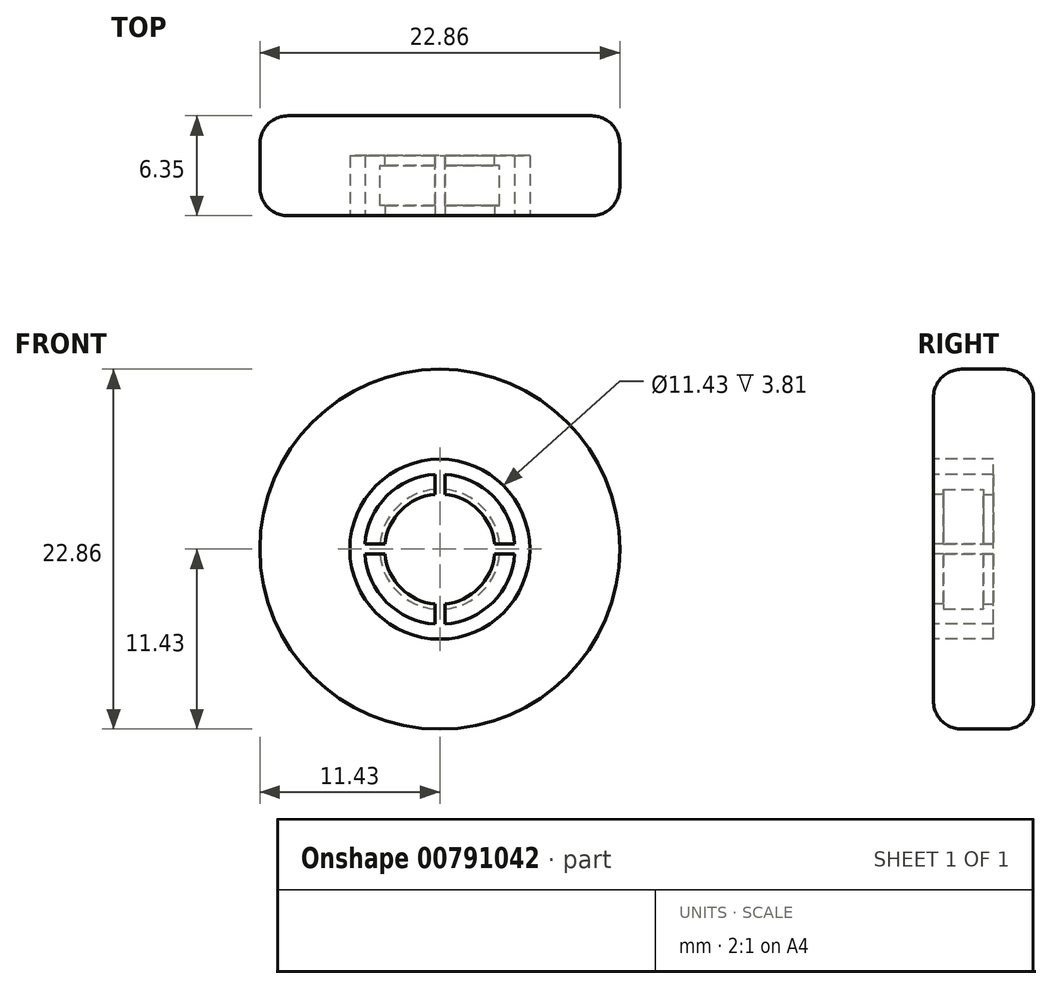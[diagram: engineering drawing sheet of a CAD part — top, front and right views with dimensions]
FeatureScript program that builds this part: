
annotation { "Feature Type Name" : "Feature", "Feature Type Description" : "" }
export const myFeature = defineFeature(function(context is Context, id is Id, definition is map)
    precondition{}
    {
        {
            var Q0;
            Q0=qCreatedBy(makeId("Front.planeOp"),FACE);
            var sketch = newSketch(context, id + "F0", { "sketchPlane" : qUnion([Q0])});
            skCircle(sketch, "E0", {"center": v(0, 0) * mm, "radius": 11.43 * mm});
            skSolve(sketch);
        }
        {
            var Q0;
            Q0=makeQuery(id+"F0.imprint","IMPRINT",FACE,{"disambiguationData":[TD([[makeQuery(id+"F0.imprint","IMPRINT",EDGE,{"derivedFrom":sQuery(id+"F0.wireOp",EDGE,"E0")}),1.0]])]});
            extrude(context, id + "F1", {"entities" : qUnion([Q0]), "depth" : 6.35 * mm, "offsetDistance" : 25.4 * mm});
        }
        {
            var Q0;
            Q0=makeQuery(id+"F1.opExtrude","CAP_FACE",FACE,{"disambiguationData":[OSD([sQuery(id+"F0.wireOp",EDGE,"E0")])],"isStart":false});
            var sketch = newSketch(context, id + "F2", { "sketchPlane" : qUnion([Q0])});
            skCircle(sketch, "E1", {"center": v(0, 0) * mm, "radius": 3.5 * mm});
            skSolve(sketch);
        }
        {
            var Q0;
            Q0=makeQuery(id+"F2.imprint","IMPRINT",FACE,{"disambiguationData":[TD([[makeQuery(id+"F2.imprint","IMPRINT",EDGE,{"derivedFrom":sQuery(id+"F2.wireOp",EDGE,"E1")}),1.0]])]});
            extrude(context, id + "F3", {"entities" : qUnion([Q0]), "operationType" : NewBodyOperationType.REMOVE, "oppositeDirection" : true, "depth" : 3.8 * mm, "offsetDistance" : 25.4 * mm});
        }
        {
            var Q0;
            Q0=makeQuery(id+"F1.opExtrude","CAP_FACE",FACE,{"disambiguationData":[OSD([sQuery(id+"F0.wireOp",EDGE,"E0")])],"isStart":false});
            var sketch = newSketch(context, id + "F4", { "sketchPlane" : qUnion([Q0])});
            skCircle(sketch, "E2", {"center": v(0, 0) * mm, "radius": 5.72 * mm});
            skCircle(sketch, "E3", {"center": v(0, 0) * mm, "radius": 4.76 * mm});
            skSolve(sketch);
        }
        {
            var Q0;
            Q0=makeQuery(id+"F4.imprint","IMPRINT",FACE,{"disambiguationData":[TD([[makeQuery(id+"F4.imprint","IMPRINT",EDGE,{"derivedFrom":sQuery(id+"F4.wireOp",EDGE,"E2")}),1.0]])]});
            extrude(context, id + "F5", {"entities" : qUnion([Q0]), "operationType" : NewBodyOperationType.REMOVE, "oppositeDirection" : true, "depth" : 3.8 * mm, "offsetDistance" : 25.4 * mm});
        }
        {
            var Q0;
            Q0=makeQuery(id+"F1.opExtrude","CAP_FACE",FACE,{"disambiguationData":[OSD([sQuery(id+"F0.wireOp",EDGE,"E0")])],"isStart":false});
            var sketch = newSketch(context, id + "F6", { "sketchPlane" : qUnion([Q0])});
            skCircle(sketch, "E4", {"center": v(0, 0) * mm, "radius": 4.45 * mm});
            skLineSegment(sketch, "E5.bottom", {"start": v(0.32, 4.76) * mm, "end": v(-0.32, 4.76) * mm});
            skLineSegment(sketch, "E5.top", {"start": v(0.32, 2.22) * mm, "end": v(-0.32, 2.22) * mm});
            skLineSegment(sketch, "E5.left", {"start": v(0.32, 4.76) * mm, "end": v(0.32, 2.22) * mm});
            skLineSegment(sketch, "E5.right", {"start": v(-0.32, 4.76) * mm, "end": v(-0.32, 2.22) * mm});
            skPoint(sketch, "E5.middle", {"position": v(0, 3.5) * mm});
            skLineSegment(sketch, "E6.bottom", {"start": v(-4.76, 0.32) * mm, "end": v(-2.22, 0.32) * mm});
            skLineSegment(sketch, "E6.top", {"start": v(-4.76, -0.32) * mm, "end": v(-2.22, -0.32) * mm});
            skLineSegment(sketch, "E6.left", {"start": v(-4.76, 0.32) * mm, "end": v(-4.76, -0.32) * mm});
            skLineSegment(sketch, "E6.right", {"start": v(-2.22, 0.32) * mm, "end": v(-2.22, -0.32) * mm});
            skPoint(sketch, "E6.middle", {"position": v(-3.5, 0) * mm});
            skLineSegment(sketch, "E7.bottom", {"start": v(4.76, 0.32) * mm, "end": v(2.22, 0.32) * mm});
            skLineSegment(sketch, "E7.top", {"start": v(4.76, -0.32) * mm, "end": v(2.22, -0.32) * mm});
            skLineSegment(sketch, "E7.left", {"start": v(4.76, 0.32) * mm, "end": v(4.76, -0.32) * mm});
            skLineSegment(sketch, "E7.right", {"start": v(2.22, 0.32) * mm, "end": v(2.22, -0.32) * mm});
            skPoint(sketch, "E7.middle", {"position": v(3.5, 0) * mm});
            skLineSegment(sketch, "E8.bottom", {"start": v(-0.32, -4.76) * mm, "end": v(0.32, -4.76) * mm});
            skLineSegment(sketch, "E8.top", {"start": v(-0.32, -2.22) * mm, "end": v(0.32, -2.22) * mm});
            skLineSegment(sketch, "E8.left", {"start": v(-0.32, -4.76) * mm, "end": v(-0.32, -2.22) * mm});
            skLineSegment(sketch, "E8.right", {"start": v(0.32, -4.76) * mm, "end": v(0.32, -2.22) * mm});
            skPoint(sketch, "E8.middle", {"position": v(0, -3.5) * mm});
            skSolve(sketch);
        }
        {
            var Q0;
            {var subQ0=sQuery(id+"F6.wireOp",EDGE,"E5.left");var subQ1=sQuery(id+"F6.wireOp",EDGE,"E4");var subQ2=makeQuery(id+"F6.imprint","INTERSECT",VERTEX,{"derivedFrom":[subQ1,subQ0]});Q0=makeQuery(id+"F6.imprint","IMPRINT",FACE,{"disambiguationData":[TD([[makeQuery(id+"F6.imprint","IMPRINT",EDGE,{"disambiguationData":[TD([[subQ2,-1.0]])],"derivedFrom":subQ1}),1.0]])]});}
            var Q1;
            {var subQ0=sQuery(id+"F6.wireOp",EDGE,"E6.bottom");var subQ1=sQuery(id+"F6.wireOp",EDGE,"E4");var subQ2=makeQuery(id+"F6.imprint","INTERSECT",VERTEX,{"derivedFrom":[subQ1,subQ0]});Q1=makeQuery(id+"F6.imprint","IMPRINT",FACE,{"disambiguationData":[TD([[makeQuery(id+"F6.imprint","IMPRINT",EDGE,{"disambiguationData":[TD([[subQ2,-1.0]])],"derivedFrom":subQ1}),1.0]])]});}
            var Q2;
            {var subQ0=sQuery(id+"F6.wireOp",EDGE,"E7.bottom");var subQ1=sQuery(id+"F6.wireOp",EDGE,"E4");var subQ2=makeQuery(id+"F6.imprint","INTERSECT",VERTEX,{"derivedFrom":[subQ1,subQ0]});Q2=makeQuery(id+"F6.imprint","IMPRINT",FACE,{"disambiguationData":[TD([[makeQuery(id+"F6.imprint","IMPRINT",EDGE,{"disambiguationData":[TD([[subQ2,1.0]])],"derivedFrom":subQ1}),1.0]])]});}
            var Q3;
            {var subQ0=sQuery(id+"F6.wireOp",EDGE,"E8.left");var subQ1=sQuery(id+"F6.wireOp",EDGE,"E4");var subQ2=makeQuery(id+"F6.imprint","INTERSECT",VERTEX,{"derivedFrom":[subQ1,subQ0]});Q3=makeQuery(id+"F6.imprint","IMPRINT",FACE,{"disambiguationData":[TD([[makeQuery(id+"F6.imprint","IMPRINT",EDGE,{"disambiguationData":[TD([[subQ2,-1.0]])],"derivedFrom":subQ1}),1.0]])]});}
            var Q4;
            {var subQ2=sQuery(id+"F6.wireOp",EDGE,"E5.left");var subQ4=sQuery(id+"F6.wireOp",EDGE,"E4");var subQ5=makeQuery(id+"F6.imprint","INTERSECT",VERTEX,{"derivedFrom":[subQ4,subQ2]});Q4=makeQuery(id+"F6.imprint","IMPRINT",FACE,{"disambiguationData":[TD([[makeQuery(id+"F6.imprint","IMPRINT",EDGE,{"disambiguationData":[TD([[subQ5,-1.0]])],"derivedFrom":subQ4}),-1.0]])]});}
            var Q5;
            {var subQ0=sQuery(id+"F6.wireOp",EDGE,"E6.bottom");var subQ5=sQuery(id+"F6.wireOp",EDGE,"E4");var subQ8=makeQuery(id+"F6.imprint","INTERSECT",VERTEX,{"derivedFrom":[subQ5,subQ0]});Q5=makeQuery(id+"F6.imprint","IMPRINT",FACE,{"disambiguationData":[TD([[makeQuery(id+"F6.imprint","IMPRINT",EDGE,{"disambiguationData":[TD([[subQ8,-1.0]])],"derivedFrom":subQ5}),-1.0]])]});}
            var Q6;
            {var subQ0=sQuery(id+"F6.wireOp",EDGE,"E7.bottom");var subQ5=sQuery(id+"F6.wireOp",EDGE,"E4");var subQ8=makeQuery(id+"F6.imprint","INTERSECT",VERTEX,{"derivedFrom":[subQ5,subQ0]});Q6=makeQuery(id+"F6.imprint","IMPRINT",FACE,{"disambiguationData":[TD([[makeQuery(id+"F6.imprint","IMPRINT",EDGE,{"disambiguationData":[TD([[subQ8,1.0]])],"derivedFrom":subQ5}),-1.0]])]});}
            var Q7;
            {var subQ2=sQuery(id+"F6.wireOp",EDGE,"E8.left");var subQ5=sQuery(id+"F6.wireOp",EDGE,"E4");var subQ8=makeQuery(id+"F6.imprint","INTERSECT",VERTEX,{"derivedFrom":[subQ5,subQ2]});Q7=makeQuery(id+"F6.imprint","IMPRINT",FACE,{"disambiguationData":[TD([[makeQuery(id+"F6.imprint","IMPRINT",EDGE,{"disambiguationData":[TD([[subQ8,-1.0]])],"derivedFrom":subQ5}),-1.0]])]});}
            extrude(context, id + "F7", {"entities" : qUnion([Q0, Q1, Q2, Q3, Q4, Q5, Q6, Q7]), "operationType" : NewBodyOperationType.REMOVE, "oppositeDirection" : true, "depth" : 3.8 * mm, "offsetDistance" : 25.4 * mm});
        }
        {
            var Q0;
            {var subQ0=sQuery(id+"F6.wireOp",EDGE,"E4");var subQ1=sQuery(id+"F2.wireOp",EDGE,"E1");Q0=makeQuery(id+"F7.boolean.opBoolean","MERGE",FACE,{"derivedFrom":[makeQuery(id+"F3.boolean.opBoolean","COPY",FACE,{"derivedFrom":makeQuery(id+"F3.opExtrude","CAP_FACE",FACE,{"disambiguationData":[OSD([subQ1])],"isStart":false})}),makeQuery(id+"F5.boolean.opBoolean","COPY",FACE,{"derivedFrom":makeQuery(id+"F5.opExtrude","CAP_FACE",FACE,{"disambiguationData":[OSD([sQuery(id+"F4.wireOp",EDGE,"E2"),sQuery(id+"F4.wireOp",EDGE,"E3")])],"isStart":false})}),makeQuery(id+"F7.opExtrude","CAP_FACE",FACE,{"disambiguationData":[OSD([subQ1,subQ0,sQuery(id+"F6.wireOp",EDGE,"E5.left"),sQuery(id+"F6.wireOp",EDGE,"E5.right")])],"isStart":false}),makeQuery(id+"F7.opExtrude","CAP_FACE",FACE,{"disambiguationData":[OSD([subQ1,subQ0,sQuery(id+"F6.wireOp",EDGE,"E6.bottom"),sQuery(id+"F6.wireOp",EDGE,"E6.top")])],"isStart":false}),makeQuery(id+"F7.opExtrude","CAP_FACE",FACE,{"disambiguationData":[OSD([subQ1,subQ0,sQuery(id+"F6.wireOp",EDGE,"E8.left"),sQuery(id+"F6.wireOp",EDGE,"E8.right")])],"isStart":false}),makeQuery(id+"F7.opExtrude","CAP_FACE",FACE,{"disambiguationData":[OSD([subQ1,subQ0,sQuery(id+"F6.wireOp",EDGE,"E7.bottom"),sQuery(id+"F6.wireOp",EDGE,"E7.top")])],"isStart":false})]});}
            var sketch = newSketch(context, id + "F8", { "sketchPlane" : qUnion([Q0])});
            skCircle(sketch, "E9", {"center": v(0, 0) * mm, "radius": 3.81 * mm});
            skSolve(sketch);
        }
        {
            var Q0;
            Q0 = qSketchRegion(id + "F8", true);
            extrude(context, id + "F9", {"entities" : qUnion([Q0]), "operationType" : NewBodyOperationType.REMOVE, "depth" : 3.17 * mm, "offsetDistance" : 25.4 * mm});
        }
        {
            var Q0;
            Q0=makeQuery(id+"F1.opExtrude","CAP_EDGE",EDGE,{"disambiguationData":[OSD([sQuery(id+"F0.wireOp",EDGE,"E0")])],"isStart":false});
            var Q1;
            Q1=makeQuery(id+"F1.opExtrude","CAP_EDGE",EDGE,{"disambiguationData":[OSD([sQuery(id+"F0.wireOp",EDGE,"E0")])],"isStart":true});
            fillet(context, id + "F10", {"entities" : qUnion([Q0, Q1]), "radius" : 1.78 * mm, "tangentPropagation" : true, "allowEdgeOverflow" : false});
        }
        {
            var Q0;
            {var subQ0=sQuery(id+"F8.wireOp",EDGE,"E9");var subQ1=sQuery(id+"F6.wireOp",EDGE,"E8.right");var subQ2=makeQuery(id+"F7.boolean.opBoolean","COPY",EDGE,{"derivedFrom":makeQuery(id+"F7.opExtrude","CAP_EDGE",EDGE,{"disambiguationData":[OSD([subQ1])],"isStart":false})});var subQ3=makeQuery(id+"F8.imprint","INTERSECT",VERTEX,{"derivedFrom":[subQ2,subQ0]});Q0=makeQuery(id+"F8.imprint","IMPRINT",FACE,{"disambiguationData":[TD([[makeQuery(id+"F8.imprint","IMPRINT",EDGE,{"disambiguationData":[TD([[subQ3,-1.0]])],"derivedFrom":subQ0}),1.0]])]});}
            var Q1;
            {var subQ0=sQuery(id+"F8.wireOp",EDGE,"E9");var subQ1=sQuery(id+"F6.wireOp",EDGE,"E5.left");var subQ2=makeQuery(id+"F7.boolean.opBoolean","COPY",EDGE,{"derivedFrom":makeQuery(id+"F7.opExtrude","CAP_EDGE",EDGE,{"disambiguationData":[OSD([subQ1])],"isStart":false})});var subQ3=makeQuery(id+"F8.imprint","INTERSECT",VERTEX,{"derivedFrom":[subQ2,subQ0]});Q1=makeQuery(id+"F8.imprint","IMPRINT",FACE,{"disambiguationData":[TD([[makeQuery(id+"F8.imprint","IMPRINT",EDGE,{"disambiguationData":[TD([[subQ3,1.0]])],"derivedFrom":subQ0}),1.0]])]});}
            var Q2;
            {var subQ0=sQuery(id+"F8.wireOp",EDGE,"E9");var subQ1=sQuery(id+"F6.wireOp",EDGE,"E5.right");var subQ2=makeQuery(id+"F7.boolean.opBoolean","COPY",EDGE,{"derivedFrom":makeQuery(id+"F7.opExtrude","CAP_EDGE",EDGE,{"disambiguationData":[OSD([subQ1])],"isStart":false})});var subQ3=makeQuery(id+"F8.imprint","INTERSECT",VERTEX,{"derivedFrom":[subQ2,subQ0]});Q2=makeQuery(id+"F8.imprint","IMPRINT",FACE,{"disambiguationData":[TD([[makeQuery(id+"F8.imprint","IMPRINT",EDGE,{"disambiguationData":[TD([[subQ3,-1.0]])],"derivedFrom":subQ0}),1.0]])]});}
            var Q3;
            {var subQ0=sQuery(id+"F8.wireOp",EDGE,"E9");var subQ1=sQuery(id+"F6.wireOp",EDGE,"E6.top");var subQ2=makeQuery(id+"F7.boolean.opBoolean","COPY",EDGE,{"derivedFrom":makeQuery(id+"F7.opExtrude","CAP_EDGE",EDGE,{"disambiguationData":[OSD([subQ1])],"isStart":false})});var subQ3=makeQuery(id+"F8.imprint","INTERSECT",VERTEX,{"derivedFrom":[subQ2,subQ0]});Q3=makeQuery(id+"F8.imprint","IMPRINT",FACE,{"disambiguationData":[TD([[makeQuery(id+"F8.imprint","IMPRINT",EDGE,{"disambiguationData":[TD([[subQ3,-1.0]])],"derivedFrom":subQ0}),1.0]])]});}
            extrude(context, id + "F11", {"entities" : qUnion([Q0, Q1, Q2, Q3]), "operationType" : NewBodyOperationType.ADD, "depth" : 0.64 * mm, "offsetDistance" : 25.4 * mm});
        }
    });
